# Revit family: Oslo 100 ETL
name_source: partatom
category: Lighting Fixtures
revit_build: Autodesk Revit 2018 (Build: 20170223_1515(x64)
units: mm (PartAtom-declared; Revit-internal decimal feet)

## family parameters
Always vertical = Yes
Cut with Voids When Loaded = No
Host = Wall
Light Source = Yes
OmniClass Number = 23.80.70.00
OmniClass Title = Lighting
Part Type = Normal
Room Calculation Point = No
Round Connector Dimension = Use Diameter
Shared = No

## types (3) — shared parameters
ADA compliant = NO
Color Filter = 16777215
Dimmable = No
Dimming Lamp Color Temperature Shift = <None>
Driver Included = Yes
Driver Required = No
Efficacy (lm/w) = 26.3
Electrical Class = 1
Emit from Line Length = 610 mm
Lamp = LED
Length of Cable Supplied = 150mm/6"
Light Source Fixed = Yes
Location rating = WET
Main Material = Metal - Aluminium
Manufacturer = Astro Lighting Ltd
Photometric Web File = 7108 OSLO 100 ies.ies
Power (Watts) = 3.4
Product Location = Outdoor
Product Name = Oslo 100
Tilt Angle = 60.00°
URL = www.astrolighting.com

## per-type parameters (varying)
| type | Main Finish | Product Code | Product SKU |
| Oslo 100 White | Textured White | 8076 | 1298010 |
| Oslo 100 Black | Textured Black | 8077 | 1298011 |
| Oslo 100 Grey | Textured Grey | 8078 | 1298012 |

## geometry (parser evidence)
native form markers: Sweep x1
no freeform markers — native parametric forms only
